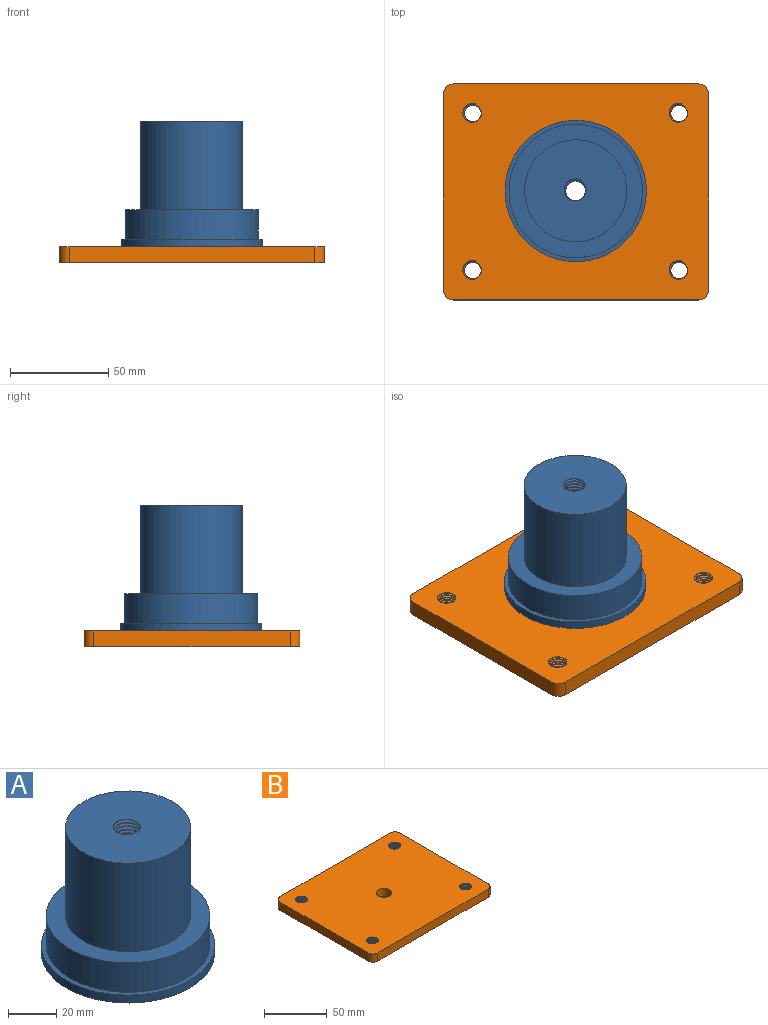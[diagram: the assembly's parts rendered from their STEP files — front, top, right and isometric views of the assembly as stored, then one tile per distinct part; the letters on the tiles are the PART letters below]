
ASSEMBLY  parts=2 mates=1
PART A: 11 faces, bbox 72.5x72.5x65.9 mm
  f0: plane 72.51x72.51mm, normal (0,0,-1), area 3974.5mm2, adj f1,f7,f8,f9,f10
  f1: cylinder r=36mm len=72mm, axis (0,0,1), area 904.8mm2, adj f0,f2
  f2: plane 72x72mm, normal (0,0,1), area 439.8mm2, adj f1,f3
  f3: cylinder r=34mm len=68mm, axis (0,0,1), area 3204.4mm2, adj f2,f4
  f4: plane 68x68mm, normal (0,0,1), area 1508mm2, adj f3,f5
  f5: cylinder r=26mm len=52mm, axis (0,0,1), area 7351.3mm2, adj f4,f6
  f6: plane 52.52x52.52mm, normal (0,0,1), area 2026.7mm2, adj f5,f7,f8,f9,f10
  f7: bspline ~65.3x14.02mm, area 1406.8mm2, adj f0,f6,f9,f10
  f8: bspline ~65.3x14.02mm, area 1411.3mm2, adj f0,f6,f9,f10
  f9: bspline ~64.68x14.21mm, area 356.6mm2, adj f0,f6,f7,f8
  f10: cylinder r=5.12mm len=64mm, axis (0,0,-1), area 463.9mm2, adj f0,f6,f7,f8
PART B: 27 faces, bbox 135.4x110.4x9.8 mm
  f0: plane 100x8mm, normal (1,0,0), area 800mm2, adj f1,f8,f9,f10
  f1: cylinder r=5mm len=8mm, axis (0,0,-1), area 62.8mm2, adj f0,f2,f9,f10
  f2: plane 125x8mm, normal (0,1,0), area 1000mm2, adj f1,f3,f9,f10
  f3: cylinder r=5mm len=8mm, axis (0,0,-1), area 62.8mm2, adj f2,f4,f9,f10
  f4: plane 100x8mm, normal (-1,0,0), area 800mm2, adj f3,f5,f9,f10
  f5: cylinder r=5mm len=8mm, axis (0,0,-1), area 62.8mm2, adj f4,f6,f9,f10
  f6: plane 125x8mm, normal (0,-1,0), area 1000mm2, adj f5,f8,f9,f10
  f7: cylinder r=6.25mm len=12.5mm, axis (0,0,-1), area 314.2mm2, adj f9,f10
  f8: cylinder r=5mm len=8mm, axis (0,0,-1), area 62.8mm2, adj f0,f6,f9,f10
  f9: plane 135.44x110.44mm, normal (0,0,1), area 14437.5mm2, adj f0,f1,f2,f3,f4,f5,f6,f7
  f10: plane 135.44x110.44mm, normal (0,0,-1), area 14437.6mm2, adj f0,f1,f2,f3,f4,f5,f6,f7
  f11: bspline ~11.69x10.12mm, area 146.5mm2, adj f9,f10,f13,f14
  f12: bspline ~11.69x10.12mm, area 146.4mm2, adj f9,f10,f13,f14
  f13: bspline ~11.85x10.26mm, area 37.1mm2, adj f9,f10,f11,f12
  f14: cylinder r=4.25mm len=8.5mm, axis (0,0,1), area 51.7mm2, adj f9,f10,f11,f12
  f15: bspline ~11.69x10.12mm, area 146.5mm2, adj f9,f10,f17,f18
  f16: bspline ~11.69x10.12mm, area 146.4mm2, adj f9,f10,f17,f18
  f17: bspline ~11.85x10.26mm, area 37.1mm2, adj f9,f10,f15,f16
  f18: cylinder r=4.25mm len=8.5mm, axis (0,0,1), area 51.7mm2, adj f9,f10,f15,f16
  f19: bspline ~11.69x10.12mm, area 146.5mm2, adj f9,f10,f21,f22
  f20: bspline ~11.69x10.12mm, area 146.4mm2, adj f9,f10,f21,f22
  f21: bspline ~11.85x10.26mm, area 37.1mm2, adj f9,f10,f19,f20
  f22: cylinder r=4.25mm len=8.5mm, axis (0,0,1), area 51.7mm2, adj f9,f10,f19,f20
  f23: bspline ~11.69x10.12mm, area 146.5mm2, adj f9,f10,f25,f26
  f24: bspline ~11.69x10.12mm, area 146.4mm2, adj f9,f10,f25,f26
  f25: bspline ~11.85x10.26mm, area 37.1mm2, adj f9,f10,f23,f24
  f26: cylinder r=4.25mm len=8.5mm, axis (0,0,1), area 51.7mm2, adj f9,f10,f23,f24
PLACE A at identity fixed
PLACE B t=(-67.33,-55.49,-8)mm
MATE fastened A.f0 <-> B.f7  axis (0,0,-1) through (0.17,-0.49,0)mm
